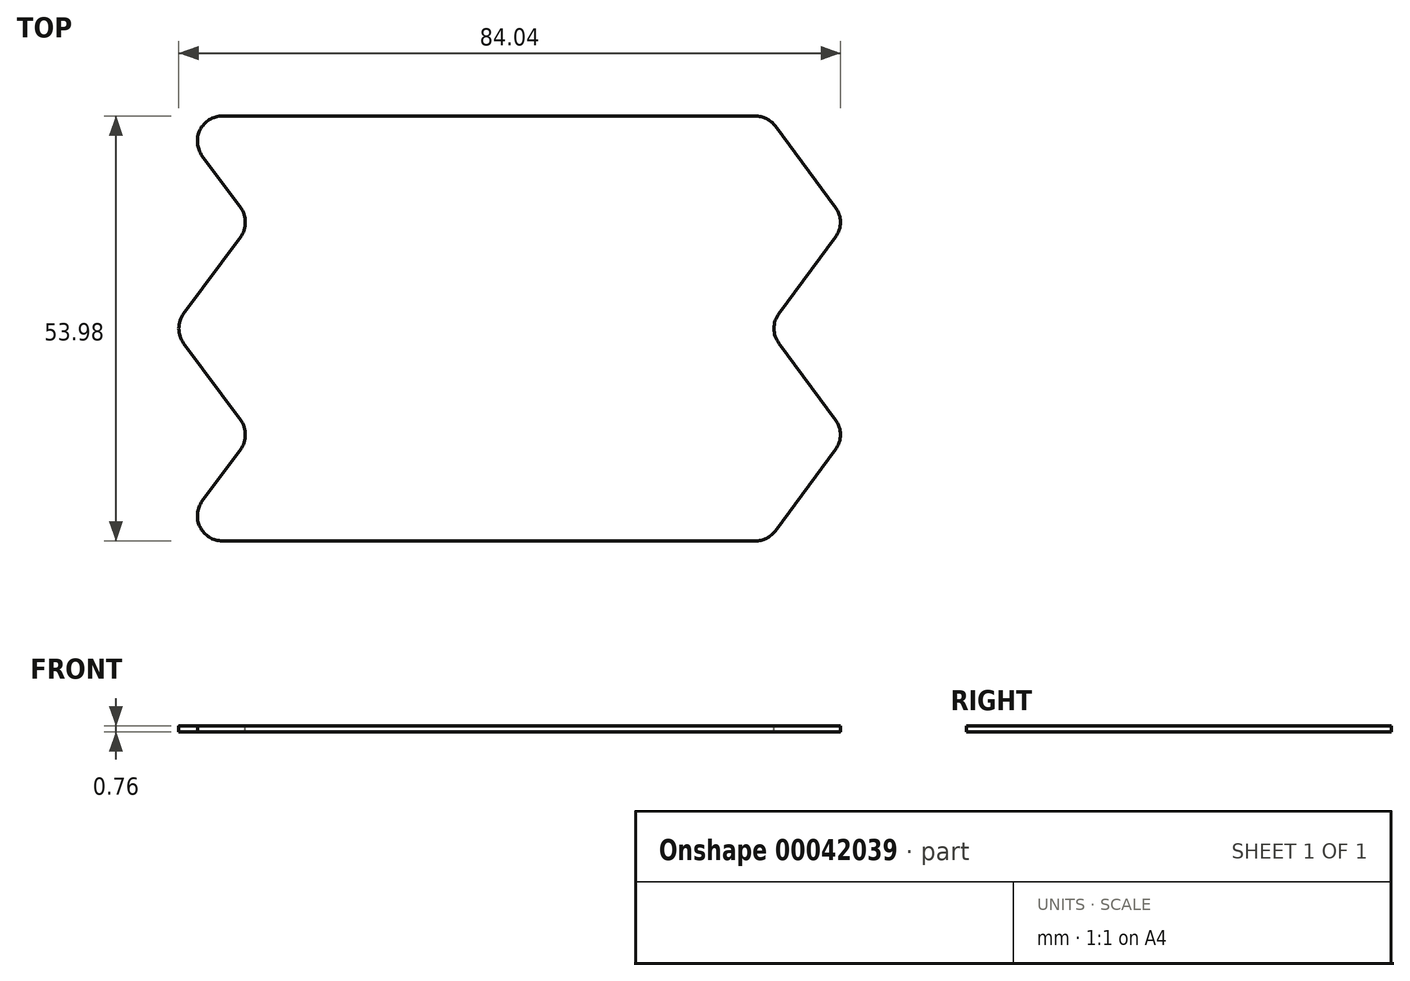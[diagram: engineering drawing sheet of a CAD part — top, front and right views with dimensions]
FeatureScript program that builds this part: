
annotation { "Feature Type Name" : "Feature", "Feature Type Description" : "" }
export const myFeature = defineFeature(function(context is Context, id is Id, definition is map)
    precondition{}
    {
        {
            var Q0;
            Q0=qCreatedBy(makeId("Top.planeOp"),FACE);
            var sketch = newSketch(context, id + "F0", { "sketchPlane" : qUnion([Q0])});
            skLineSegment(sketch, "E0.bottom", {"start": v(0, 53.98) * mm, "end": v(85.6, 53.98) * mm, "construction": true});
            skLineSegment(sketch, "E0.top", {"start": v(0, 0) * mm, "end": v(85.6, 0) * mm, "construction": true});
            skLineSegment(sketch, "E0.left", {"start": v(0, 53.98) * mm, "end": v(0, 0) * mm, "construction": true});
            skLineSegment(sketch, "E0.right", {"start": v(85.6, 53.98) * mm, "end": v(85.6, 0) * mm, "construction": true});
            skLineSegment(sketch, "E1", {"start": v(75.6, 53.98) * mm, "end": v(85.6, 40.48) * mm});
            skLineSegment(sketch, "E2", {"start": v(85.6, 40.48) * mm, "end": v(75.6, 26.99) * mm});
            skLineSegment(sketch, "E3", {"start": v(75.6, 26.99) * mm, "end": v(85.6, 13.5) * mm});
            skLineSegment(sketch, "E4", {"start": v(85.6, 13.5) * mm, "end": v(75.6, 0) * mm});
            skLineSegment(sketch, "E5", {"start": v(75.6, 0) * mm, "end": v(0, 0) * mm});
            skLineSegment(sketch, "E6", {"start": v(0, 0) * mm, "end": v(10, 13.5) * mm});
            skLineSegment(sketch, "E7", {"start": v(10, 13.5) * mm, "end": v(0, 27) * mm});
            skLineSegment(sketch, "E8", {"start": v(0, 26.99) * mm, "end": v(10, 40.48) * mm});
            skLineSegment(sketch, "E9", {"start": v(10, 40.48) * mm, "end": v(0, 53.98) * mm});
            skLineSegment(sketch, "E10", {"start": v(0, 53.98) * mm, "end": v(75.6, 53.98) * mm});
            skLineSegment(sketch, "E11", {"start": v(0, 40.48) * mm, "end": v(85.6, 40.48) * mm, "construction": true});
            skLineSegment(sketch, "E12", {"start": v(0, 13.5) * mm, "end": v(85.6, 13.5) * mm, "construction": true});
            skLineSegment(sketch, "E13", {"start": v(0, 26.99) * mm, "end": v(85.6, 26.99) * mm, "construction": true});
            skLineSegment(sketch, "E14.bottom", {"start": v(10.25, 34.75) * mm, "end": v(20.25, 34.75) * mm, "construction": true});
            skLineSegment(sketch, "E14.top", {"start": v(10.25, 25.75) * mm, "end": v(20.25, 25.75) * mm, "construction": true});
            skLineSegment(sketch, "E14.left", {"start": v(10.25, 34.75) * mm, "end": v(10.25, 25.75) * mm, "construction": true});
            skLineSegment(sketch, "E14.right", {"start": v(20.25, 34.75) * mm, "end": v(20.25, 25.75) * mm, "construction": true});
            skSolve(sketch);
        }
        {
            var Q0;
            Q0 = qSketchRegion(id + "F0", true);
            extrude(context, id + "F1", {"entities" : qUnion([Q0]), "depth" : 0.76 * mm});
        }
        {
            var Q0;
            Q0=makeQuery(id+"F1.opExtrude","SWEPT_EDGE",EDGE,{"disambiguationData":[OSD([sQuery(id+"F0.wireOp",EDGE,"E9"),sQuery(id+"F0.wireOp",EDGE,"E10")])]});
            var Q1;
            Q1=makeQuery(id+"F1.opExtrude","SWEPT_EDGE",EDGE,{"disambiguationData":[OSD([sQuery(id+"F0.wireOp",EDGE,"E8"),sQuery(id+"F0.wireOp",EDGE,"E9")])]});
            var Q2;
            Q2=makeQuery(id+"F1.opExtrude","SWEPT_EDGE",EDGE,{"disambiguationData":[OSD([sQuery(id+"F0.wireOp",EDGE,"E7"),sQuery(id+"F0.wireOp",EDGE,"E8")])]});
            var Q3;
            Q3=makeQuery(id+"F1.opExtrude","SWEPT_EDGE",EDGE,{"disambiguationData":[OSD([sQuery(id+"F0.wireOp",EDGE,"E6"),sQuery(id+"F0.wireOp",EDGE,"E7")])]});
            var Q4;
            Q4=makeQuery(id+"F1.opExtrude","SWEPT_EDGE",EDGE,{"disambiguationData":[OSD([sQuery(id+"F0.wireOp",EDGE,"E5"),sQuery(id+"F0.wireOp",EDGE,"E6")])]});
            var Q5;
            Q5=makeQuery(id+"F1.opExtrude","SWEPT_EDGE",EDGE,{"disambiguationData":[OSD([sQuery(id+"F0.wireOp",EDGE,"E1"),sQuery(id+"F0.wireOp",EDGE,"E10")])]});
            var Q6;
            Q6=makeQuery(id+"F1.opExtrude","SWEPT_EDGE",EDGE,{"disambiguationData":[OSD([sQuery(id+"F0.wireOp",EDGE,"E1"),sQuery(id+"F0.wireOp",EDGE,"E2")])]});
            var Q7;
            Q7=makeQuery(id+"F1.opExtrude","SWEPT_EDGE",EDGE,{"disambiguationData":[OSD([sQuery(id+"F0.wireOp",EDGE,"E2"),sQuery(id+"F0.wireOp",EDGE,"E3")])]});
            var Q8;
            Q8=makeQuery(id+"F1.opExtrude","SWEPT_EDGE",EDGE,{"disambiguationData":[OSD([sQuery(id+"F0.wireOp",EDGE,"E3"),sQuery(id+"F0.wireOp",EDGE,"E4")])]});
            var Q9;
            Q9=makeQuery(id+"F1.opExtrude","SWEPT_EDGE",EDGE,{"disambiguationData":[OSD([sQuery(id+"F0.wireOp",EDGE,"E4"),sQuery(id+"F0.wireOp",EDGE,"E5")])]});
            fillet(context, id + "F2", {"entities" : qUnion([Q0, Q1, Q2, Q3, Q4, Q5, Q6, Q7, Q8, Q9]), "radius" : 3.18 * mm, "tangentPropagation" : true, "allowEdgeOverflow" : false});
        }
    });
